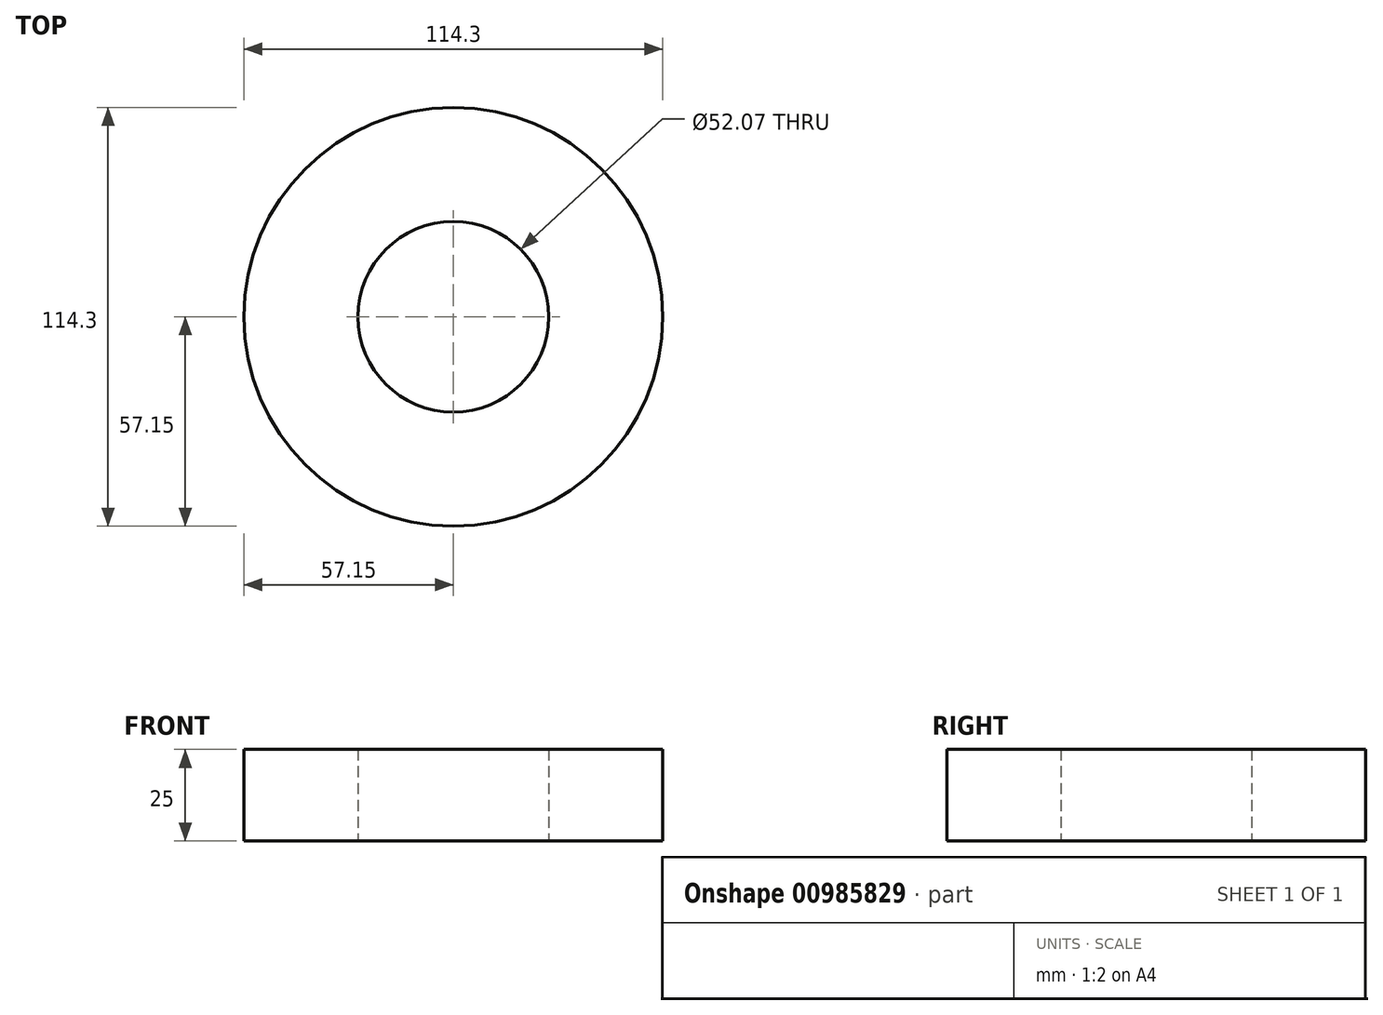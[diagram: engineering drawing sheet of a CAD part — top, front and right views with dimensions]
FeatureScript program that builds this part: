
annotation { "Feature Type Name" : "Feature", "Feature Type Description" : "" }
export const myFeature = defineFeature(function(context is Context, id is Id, definition is map)
    precondition{}
    {
        {
            var Q0;
            Q0=qCreatedBy(makeId("Top.planeOp"),FACE);
            var sketch = newSketch(context, id + "F0", { "sketchPlane" : qUnion([Q0])});
            skCircle(sketch, "E0", {"center": v(0, 0) * mm, "radius": 57.15 * mm});
            skCircle(sketch, "E1", {"center": v(0, 0) * mm, "radius": 26.04 * mm});
            skSolve(sketch);
        }
        {
            var Q0;
            Q0=makeQuery(id+"F0.imprint","IMPRINT",FACE,{"disambiguationData":[TD([[makeQuery(id+"F0.imprint","IMPRINT",EDGE,{"derivedFrom":sQuery(id+"F0.wireOp",EDGE,"E0")}),1.0]])]});
            extrude(context, id + "F1", {"entities" : qUnion([Q0]), "depth" : 25 * mm, "offsetDistance" : 25 * mm});
        }
    });
